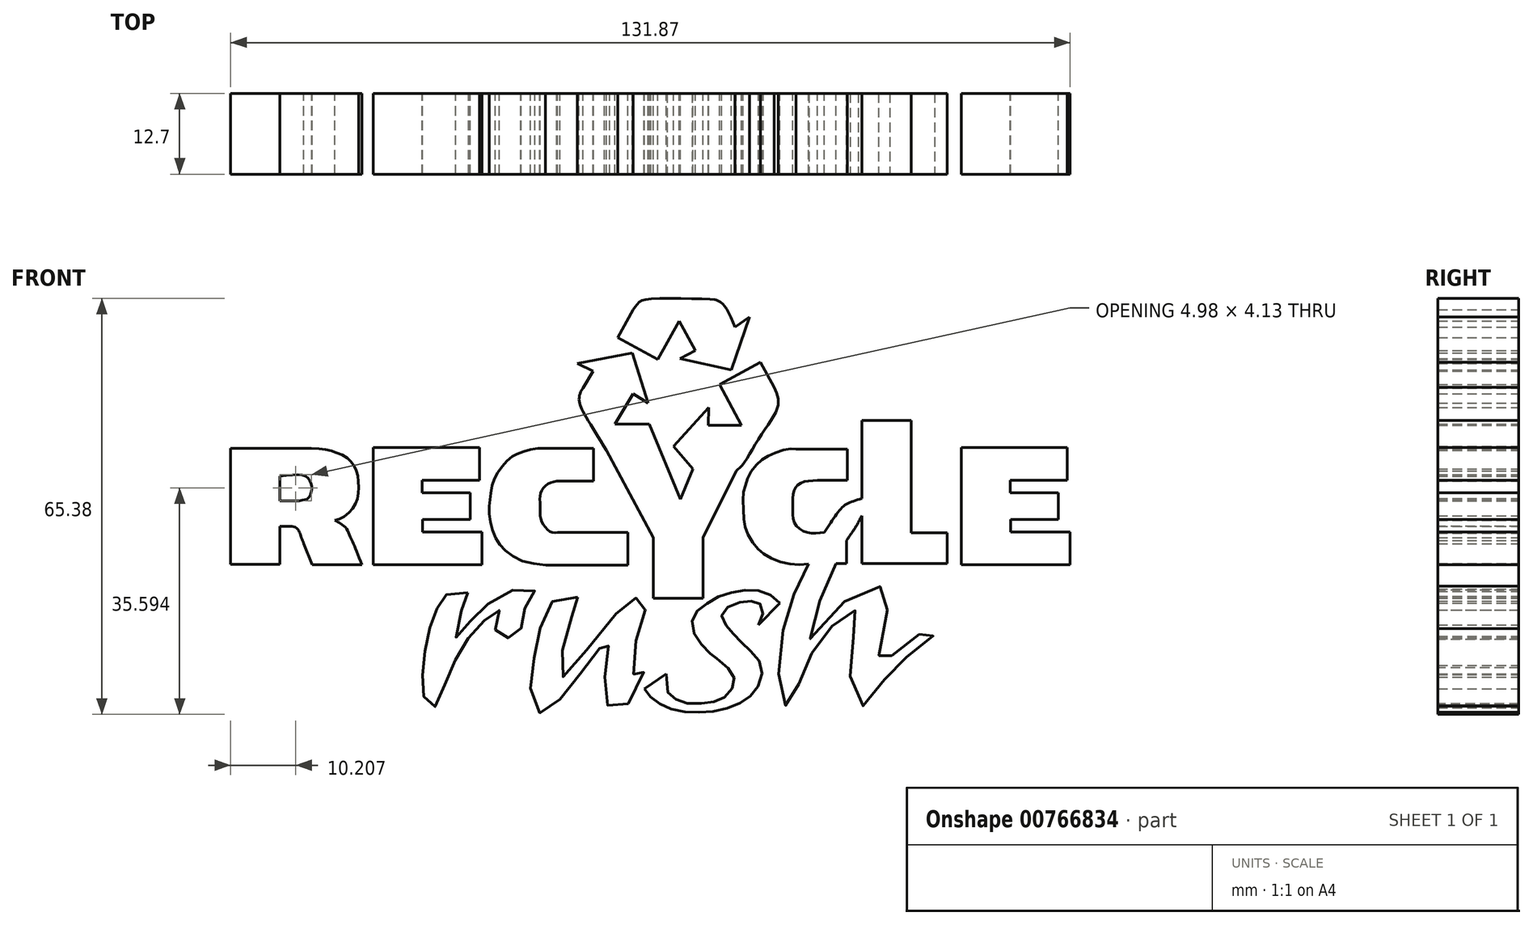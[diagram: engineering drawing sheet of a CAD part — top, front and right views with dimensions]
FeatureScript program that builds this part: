
annotation { "Feature Type Name" : "Feature", "Feature Type Description" : "" }
export const myFeature = defineFeature(function(context is Context, id is Id, definition is map)
    precondition{}
    {
        {
            var Q0;
            Q0=qCreatedBy(makeId("Front.planeOp"),FACE);
            var sketch = newSketch(context, id + "F0", { "sketchPlane" : qUnion([Q0])});
            skLineSegment(sketch, "E0", {"start": v(-43.6, 9.28) * mm, "end": v(-43.6, -9.2) * mm});
            skLineSegment(sketch, "E1", {"start": v(-43.6, -9.2) * mm, "end": v(-26.5, -9.2) * mm});
            skLineSegment(sketch, "E2", {"start": v(-26.5, -9.2) * mm, "end": v(-26.5, -4.05) * mm});
            skLineSegment(sketch, "E3", {"start": v(-26.5, -4.05) * mm, "end": v(-35.84, -4.05) * mm});
            skLineSegment(sketch, "E4", {"start": v(-35.84, -4.05) * mm, "end": v(-35.84, -2.06) * mm});
            skLineSegment(sketch, "E5", {"start": v(-35.84, -2.06) * mm, "end": v(-28.36, -2.06) * mm});
            skLineSegment(sketch, "E6", {"start": v(-28.36, -2.06) * mm, "end": v(-28.36, 2.1) * mm});
            skLineSegment(sketch, "E7", {"start": v(-28.36, 2.1) * mm, "end": v(-35.92, 2.1) * mm});
            skLineSegment(sketch, "E8", {"start": v(-35.92, 2.1) * mm, "end": v(-35.92, 4.09) * mm});
            skLineSegment(sketch, "E9", {"start": v(-35.92, 4.09) * mm, "end": v(-26.93, 4.09) * mm});
            skLineSegment(sketch, "E10", {"start": v(-26.93, 4.09) * mm, "end": v(-26.93, 9.28) * mm});
            skLineSegment(sketch, "E11", {"start": v(-26.93, 9.28) * mm, "end": v(-43.6, 9.28) * mm});
            skLineSegment(sketch, "E12.bottom", {"start": v(-66, 9.1) * mm, "end": v(-58.27, 9.1) * mm});
            skLineSegment(sketch, "E12.top", {"start": v(-66, -9.07) * mm, "end": v(-58.27, -9.07) * mm});
            skLineSegment(sketch, "E12.left", {"start": v(-66, 9.1) * mm, "end": v(-66, -9.07) * mm});
            skLineSegment(sketch, "E12.right", {"start": v(-58.27, 4.77) * mm, "end": v(-58.27, 0.85) * mm});
            skFitSpline(sketch, "E13", {"points": [v(-58.27, 9.1) * mm, v(-52.92, 9.1) * mm, v(-50.76, 8.84) * mm, v(-49.14, 8.37) * mm, v(-47.62, 7.56) * mm, v(-46.68, 6.41) * mm, v(-46.14, 5.26) * mm, v(-45.92, 3.68) * mm, v(-45.94, 1.98) * mm, v(-46.33, 0.53) * mm, v(-47.14, -0.7) * mm, v(-48.51, -1.8) * mm, v(-49.61, -2.21) * mm], "startDerivative": vector(42.38, 0.73) * mm, "endDerivative": vector(-16, -4.77) * mm});
            skFitSpline(sketch, "E14", {"points": [v(-49.61, -2.21) * mm, v(-48.87, -2.63) * mm, v(-47.91, -3.37) * mm, v(-47.2, -4.77) * mm, v(-46.68, -5.9) * mm, v(-45.37, -9.2) * mm], "startDerivative": vector(4.88, -2.66) * mm, "endDerivative": vector(4.84, -12.6) * mm});
            skLineSegment(sketch, "E15", {"start": v(-45.37, -9.2) * mm, "end": v(-53.2, -9.2) * mm});
            skLineSegment(sketch, "E16", {"start": v(-53.2, -9.2) * mm, "end": v(-54.52, -5.88) * mm});
            skFitSpline(sketch, "E17", {"points": [v(-54.52, -5.88) * mm, v(-54.98, -4.62) * mm, v(-55.4, -3.68) * mm, v(-56.17, -3.2) * mm, v(-57.92, -3.13) * mm, v(-58.27, -3.13) * mm], "startDerivative": vector(-2.08, 5.74) * mm, "endDerivative": vector(-2.94, 0.06) * mm});
            skFitSpline(sketch, "E18", {"points": [v(-58.27, 4.77) * mm, v(-54.52, 4.85) * mm, v(-53.57, 4.1) * mm, v(-53.26, 3.08) * mm, v(-53.47, 1.8) * mm, v(-53.94, 1.19) * mm, v(-54.52, 1) * mm, v(-55.73, 0.85) * mm, v(-57.42, 0.87) * mm, v(-58.27, 0.85) * mm], "startDerivative": vector(23.7, 2.7) * mm, "endDerivative": vector(-9.58, -0.43) * mm});
            skLineSegment(sketch, "E19.trimOffspring", {"start": v(-58.27, -3.13) * mm, "end": v(-58.27, -9.07) * mm});
            skLineSegment(sketch, "E20.bottom", {"start": v(33.14, 13.48) * mm, "end": v(40.9, 13.48) * mm});
            skLineSegment(sketch, "E20.top", {"start": v(33.14, -8.98) * mm, "end": v(40.9, -8.98) * mm});
            skLineSegment(sketch, "E20.left", {"start": v(33.14, 13.48) * mm, "end": v(33.14, 1.22) * mm});
            skLineSegment(sketch, "E20.right", {"start": v(40.9, 13.48) * mm, "end": v(40.9, -4.17) * mm});
            skLineSegment(sketch, "E21", {"start": v(40.9, -8.98) * mm, "end": v(46.6, -8.98) * mm});
            skLineSegment(sketch, "E22", {"start": v(46.6, -8.98) * mm, "end": v(46.6, -4.17) * mm});
            skLineSegment(sketch, "E23", {"start": v(46.6, -4.17) * mm, "end": v(40.9, -4.17) * mm});
            skLineSegment(sketch, "E24", {"start": v(30.78, -5.33) * mm, "end": v(30.78, -8.99) * mm});
            skLineSegment(sketch, "E25", {"start": v(30.78, -8.99) * mm, "end": v(29.13, -8.99) * mm});
            skFitSpline(sketch, "E26", {"points": [v(30.78, -5.33) * mm, v(31.51, -4.25) * mm, v(32.32, -3.02) * mm, v(33.14, -1.52) * mm], "startDerivative": vector(2.32, 3.42) * mm, "endDerivative": vector(2.26, 4.32) * mm});
            skFitSpline(sketch, "E27", {"points": [v(33.14, 1.22) * mm, v(31.44, 0.68) * mm, v(30.24, 0) * mm, v(29, -1.48) * mm, v(27.28, -4.1) * mm], "startDerivative": vector(-7.59, -2.16) * mm, "endDerivative": vector(-5.73, -8.86) * mm});
            skFitSpline(sketch, "E28", {"points": [v(27.28, -4.1) * mm, v(24.56, -4.1) * mm, v(22.57, -2.57) * mm, v(22.3, 0) * mm, v(22.43, 2.28) * mm, v(23.54, 3.67) * mm, v(26.18, 4.09) * mm], "startDerivative": vector(-15.66, -2.03) * mm, "endDerivative": vector(16.66, 0.52) * mm});
            skLineSegment(sketch, "E29", {"start": v(26.18, 4.09) * mm, "end": v(30.9, 4.09) * mm});
            skLineSegment(sketch, "E30", {"start": v(30.9, 4.09) * mm, "end": v(30.9, 9) * mm});
            skLineSegment(sketch, "E31", {"start": v(30.9, 9) * mm, "end": v(22.84, 9) * mm});
            skFitSpline(sketch, "E32", {"points": [v(22.84, 9) * mm, v(21.65, 9) * mm, v(19.19, 8.28) * mm, v(17.44, 7.3) * mm, v(15.82, 5.55) * mm, v(14.93, 3.5) * mm, v(14.53, 1.72) * mm, v(14.61, -1.54) * mm, v(15.04, -3.88) * mm, v(16.58, -6.42) * mm, v(18.3, -7.81) * mm, v(21.6, -9.01) * mm, v(24.77, -9.06) * mm], "startDerivative": vector(-17.73, 2.05) * mm, "endDerivative": vector(32.25, 2.73) * mm});
            skLineSegment(sketch, "E33.trimOffspring", {"start": v(33.14, -1.52) * mm, "end": v(33.14, -8.98) * mm});
            skLineSegment(sketch, "E34", {"start": v(48.78, 9.28) * mm, "end": v(48.78, -9.2) * mm});
            skLineSegment(sketch, "E35", {"start": v(48.78, -9.2) * mm, "end": v(65.88, -9.2) * mm});
            skLineSegment(sketch, "E36", {"start": v(65.88, -9.2) * mm, "end": v(65.88, -4.05) * mm});
            skLineSegment(sketch, "E37", {"start": v(65.88, -4.05) * mm, "end": v(56.54, -4.05) * mm});
            skLineSegment(sketch, "E38", {"start": v(56.54, -4.05) * mm, "end": v(56.54, -2.06) * mm});
            skLineSegment(sketch, "E39", {"start": v(56.54, -2.06) * mm, "end": v(64.03, -2.06) * mm});
            skLineSegment(sketch, "E40", {"start": v(64.03, -2.06) * mm, "end": v(64.03, 2.1) * mm});
            skLineSegment(sketch, "E41", {"start": v(64.03, 2.1) * mm, "end": v(56.47, 2.1) * mm});
            skLineSegment(sketch, "E42", {"start": v(56.47, 2.1) * mm, "end": v(56.47, 4.09) * mm});
            skLineSegment(sketch, "E43", {"start": v(56.47, 4.09) * mm, "end": v(65.46, 4.09) * mm});
            skLineSegment(sketch, "E44", {"start": v(65.46, 4.09) * mm, "end": v(65.46, 9.28) * mm});
            skLineSegment(sketch, "E45", {"start": v(65.46, 9.28) * mm, "end": v(48.78, 9.28) * mm});
            skLineSegment(sketch, "E46", {"start": v(0.38, -14.46) * mm, "end": v(8.2, -14.46) * mm});
            skLineSegment(sketch, "E47", {"start": v(8.2, -14.46) * mm, "end": v(8.2, -4.93) * mm});
            skLineSegment(sketch, "E48", {"start": v(8.2, -4.93) * mm, "end": v(13.4, 5.55) * mm});
            skLineSegment(sketch, "E49", {"start": v(0.38, -14.46) * mm, "end": v(0.38, -4.93) * mm});
            skLineSegment(sketch, "E50", {"start": v(0.38, -4.93) * mm, "end": v(-6.92, 8.81) * mm});
            skLineSegment(sketch, "E51", {"start": v(-9.07, 21.26) * mm, "end": v(-11.55, 22.45) * mm});
            skLineSegment(sketch, "E52", {"start": v(-11.55, 22.45) * mm, "end": v(-2.92, 24.1) * mm});
            skLineSegment(sketch, "E53", {"start": v(-2.92, 24.1) * mm, "end": v(-0.4, 16.23) * mm});
            skLineSegment(sketch, "E54", {"start": v(-0.4, 16.23) * mm, "end": v(-2.76, 17.67) * mm});
            skLineSegment(sketch, "E55", {"start": v(6.62, 5.86) * mm, "end": v(3.56, 9.4) * mm});
            skLineSegment(sketch, "E56", {"start": v(3.56, 9.4) * mm, "end": v(9.12, 15.52) * mm});
            skLineSegment(sketch, "E57", {"start": v(9.12, 15.52) * mm, "end": v(9.05, 12.77) * mm});
            skLineSegment(sketch, "E58", {"start": v(13.26, 28.18) * mm, "end": v(15.53, 29.74) * mm});
            skLineSegment(sketch, "E59", {"start": v(15.53, 29.74) * mm, "end": v(12.64, 21.43) * mm});
            skLineSegment(sketch, "E60", {"start": v(12.64, 21.43) * mm, "end": v(4.57, 23.2) * mm});
            skLineSegment(sketch, "E61", {"start": v(4.57, 23.2) * mm, "end": v(6.99, 24.51) * mm});
            skLineSegment(sketch, "E62", {"start": v(6.99, 24.51) * mm, "end": v(4.46, 29.15) * mm});
            skLineSegment(sketch, "E63", {"start": v(4.46, 29.15) * mm, "end": v(1.09, 23.06) * mm});
            skLineSegment(sketch, "E64", {"start": v(1.09, 23.06) * mm, "end": v(-5.2, 26.55) * mm});
            skLineSegment(sketch, "E65", {"start": v(-5.2, 26.55) * mm, "end": v(-2.8, 30.92) * mm});
            skFitSpline(sketch, "E66", {"points": [v(-2.8, 30.92) * mm, v(-1.9, 32) * mm, v(0, 32.62) * mm, v(10.1, 32.48) * mm, v(10.37, 32.41) * mm, v(11.07, 32) * mm, v(11.97, 30.92) * mm, v(13.26, 28.18) * mm], "startDerivative": vector(7.55, 10.2) * mm, "endDerivative": vector(7.62, -17.7) * mm});
            skLineSegment(sketch, "E67", {"start": v(-2.76, 17.67) * mm, "end": v(-5.63, 12.96) * mm});
            skLineSegment(sketch, "E68", {"start": v(-5.63, 12.96) * mm, "end": v(-0.23, 12.96) * mm});
            skLineSegment(sketch, "E69", {"start": v(-0.23, 12.96) * mm, "end": v(4.65, 1.14) * mm});
            skLineSegment(sketch, "E70", {"start": v(4.65, 1.14) * mm, "end": v(6.62, 5.86) * mm});
            skLineSegment(sketch, "E71", {"start": v(-9.07, 21.26) * mm, "end": v(-10.66, 18.61) * mm});
            skFitSpline(sketch, "E72", {"points": [v(-10.66, 18.61) * mm, v(-11.08, 17.83) * mm, v(-11.23, 16.46) * mm, v(-10.66, 15) * mm, v(-6.92, 8.81) * mm], "startDerivative": vector(-3.02, -4.47) * mm, "endDerivative": vector(10.8, -16.46) * mm});
            skLineSegment(sketch, "E73", {"start": v(9.05, 12.77) * mm, "end": v(14.27, 12.77) * mm});
            skLineSegment(sketch, "E74", {"start": v(14.27, 12.77) * mm, "end": v(10.8, 19.12) * mm});
            skLineSegment(sketch, "E75", {"start": v(10.8, 19.12) * mm, "end": v(17.24, 22.62) * mm});
            skLineSegment(sketch, "E76", {"start": v(17.24, 22.62) * mm, "end": v(19.38, 18.68) * mm});
            skFitSpline(sketch, "E77", {"points": [v(19.38, 18.68) * mm, v(19.99, 17.12) * mm, v(19.77, 15.13) * mm, v(17.18, 10.97) * mm, v(14.48, 6.6) * mm, v(13.4, 5.55) * mm], "startDerivative": vector(4.81, -9.86) * mm, "endDerivative": vector(-7.04, -5.45) * mm});
            skLineSegment(sketch, "E78", {"start": v(-9, 4) * mm, "end": v(-9, 9.15) * mm});
            skLineSegment(sketch, "E79", {"start": v(-9, 9.15) * mm, "end": v(-16.56, 9.15) * mm});
            skLineSegment(sketch, "E80", {"start": v(-9, 4) * mm, "end": v(-14.75, 4) * mm});
            skLineSegment(sketch, "E81", {"start": v(-3.63, -4.1) * mm, "end": v(-3.63, -9.2) * mm});
            skLineSegment(sketch, "E82", {"start": v(-3.63, -9.2) * mm, "end": v(-16.5, -9.2) * mm});
            skLineSegment(sketch, "E83", {"start": v(-3.63, -4.1) * mm, "end": v(-14.63, -4.1) * mm});
            skFitSpline(sketch, "E84", {"points": [v(-14.63, -4.1) * mm, v(-15.53, -4.1) * mm, v(-16.47, -3.4) * mm, v(-17.16, -2.3) * mm, v(-17.4, -1.07) * mm, v(-17.4, 0.5) * mm, v(-17.36, 1.84) * mm, v(-16.86, 2.87) * mm, v(-16.05, 3.6) * mm, v(-14.75, 4) * mm], "startDerivative": vector(-9.51, -1.43) * mm, "endDerivative": vector(11.9, 2.65) * mm});
            skFitSpline(sketch, "E85", {"points": [v(-16.56, 9.15) * mm, v(-18.32, 9.04) * mm, v(-19.92, 8.6) * mm, v(-21.2, 8.17) * mm, v(-22.05, 7.6) * mm, v(-23.24, 6.43) * mm, v(-24.19, 5.01) * mm, v(-24.86, 3.59) * mm, v(-25.15, 1.83) * mm, v(-25.32, 0.61) * mm, v(-25.38, -1.06) * mm, v(-25.04, -3.08) * mm, v(-24.26, -5.2) * mm, v(-23.03, -6.7) * mm, v(-20.68, -8.39) * mm, v(-16.5, -9.2) * mm], "startDerivative": vector(-27.54, -0.28) * mm, "endDerivative": vector(44.63, -4.63) * mm});
            skFitSpline(sketch, "E86", {"points": [v(29.13, -8.99) * mm, v(27.62, -12.44) * mm, v(25.92, -16.62) * mm, v(24.87, -20.93) * mm, v(27.35, -17.66) * mm, v(32.06, -14) * mm, v(35.2, -12.57) * mm, v(36.83, -12.94) * mm, v(37.55, -14.38) * mm, v(37.07, -16.59) * mm, v(36.3, -20.27) * mm, v(35.9, -25.33) * mm, v(36.71, -24.65) * mm, v(38.24, -23.09) * mm, v(40.4, -21.3) * mm, v(42.76, -19.74) * mm, v(43.92, -19.22) * mm, v(44.58, -19.66) * mm, v(44.25, -20.5) * mm, v(42.09, -22.05) * mm, v(40.04, -23.82) * mm, v(38.7, -25.1) * mm, v(36.93, -27.03) * mm, v(34.94, -29.42) * mm, v(33.5, -31.3) * mm, v(31.95, -30.58) * mm, v(31.34, -27.09) * mm, v(31.4, -23.38) * mm, v(31.95, -20) * mm, v(32.59, -17.43) * mm, v(32.4, -16.47) * mm, v(31.5, -16.42) * mm, v(29.82, -17.38) * mm, v(28.2, -19.1) * mm, v(26.57, -21.1) * mm, v(25.14, -23.4) * mm, v(24.18, -25.3) * mm, v(23.18, -28.22) * mm, v(22.46, -30.75) * mm, v(21.65, -31.37) * mm, v(20.65, -30.8) * mm, v(20.17, -28.17) * mm, v(20.12, -24.64) * mm, v(20.7, -19.86) * mm, v(21.37, -17.28) * mm, v(22.57, -13.68) * mm, v(23.75, -10.96) * mm, v(24.77, -9.06) * mm], "startDerivative": vector(-58.73, -135.62) * mm, "endDerivative": vector(52.61, 93.78) * mm});
            skFitSpline(sketch, "E87", {"points": [v(2.43, -26.29) * mm, v(2.57, -27.75) * mm, v(2.64, -29.06) * mm, v(3.65, -30.14) * mm, v(5.68, -30.96) * mm, v(8.66, -30.89) * mm, v(10.75, -30.41) * mm, v(12.38, -29.2) * mm, v(13.12, -27.44) * mm, v(12.62, -25.92) * mm, v(10.26, -23.78) * mm, v(9.54, -23.31) * mm, v(7.91, -21.62) * mm, v(6.63, -19.46) * mm, v(6.76, -17.09) * mm, v(8.18, -15.74) * mm, v(10.35, -14.32) * mm, v(13.12, -13.44) * mm, v(15.96, -13.17) * mm, v(18.47, -13.7) * mm, v(20.3, -15.2) * mm], "startDerivative": vector(5.07, -36.06) * mm, "endDerivative": vector(32.32, -32.5) * mm});
            skLineSegment(sketch, "E88", {"start": v(20.3, -15.2) * mm, "end": v(16.9, -18.65) * mm});
            skLineSegment(sketch, "E89", {"start": v(2.43, -26.29) * mm, "end": v(-1.02, -28.66) * mm});
            skFitSpline(sketch, "E90", {"points": [v(-1.02, -28.66) * mm, v(0, -29.94) * mm, v(1.7, -31.16) * mm, v(4.2, -32.1) * mm, v(7.44, -32.38) * mm, v(10.55, -32.1) * mm, v(13.6, -31.08) * mm, v(15.71, -29.76) * mm, v(17.13, -27.75) * mm, v(17.38, -25.07) * mm, v(15.76, -22.84) * mm, v(14.05, -21.16) * mm, v(12.58, -19.6) * mm, v(11.43, -18.04) * mm, v(11.3, -16.55) * mm, v(13.4, -15.26) * mm, v(15.42, -14.92) * mm, v(16.98, -15.14) * mm, v(17.65, -16.55) * mm, v(16.9, -18.65) * mm], "startDerivative": vector(20.7, -29.89) * mm, "endDerivative": vector(-19.13, -40.14) * mm});
            skFitSpline(sketch, "E91", {"points": [v(-28.72, -13.56) * mm, v(-31.34, -13.56) * mm, v(-32.9, -14.55) * mm, v(-33.56, -16.05) * mm, v(-34.41, -18.14) * mm, v(-35.13, -21.02) * mm, v(-35.72, -24.36) * mm, v(-35.85, -27.3) * mm, v(-35.66, -29.8) * mm, v(-34.6, -31.56) * mm, v(-33.63, -31.23) * mm, v(-32.32, -27.9) * mm, v(-30.75, -24.3) * mm, v(-28.98, -21.15) * mm, v(-26.95, -18.73) * mm, v(-24.6, -16.7) * mm, v(-23.81, -16.31) * mm, v(-24.34, -18.14) * mm, v(-24.14, -20.17) * mm, v(-23.03, -20.63) * mm, v(-20.54, -20.3) * mm, v(-20.41, -18.4) * mm, v(-19.82, -16.18) * mm, v(-18.7, -13.7) * mm, v(-18.19, -13.17) * mm, v(-22.05, -13.24) * mm, v(-25.65, -15.4) * mm, v(-27.94, -17.5) * mm, v(-30.49, -20.76) * mm, v(-30.3, -18.34) * mm, v(-28.98, -14.61) * mm, v(-28.72, -13.56) * mm]});
            skFitSpline(sketch, "E92", {"points": [v(-11.44, -14.27) * mm, v(-13.85, -14.41) * mm, v(-15.17, -14.76) * mm, v(-16.55, -16.18) * mm, v(-17.33, -18.88) * mm, v(-17.92, -21.39) * mm, v(-18.37, -23.94) * mm, v(-18.7, -26.3) * mm, v(-18.9, -29) * mm, v(-18.46, -31.06) * mm, v(-17.38, -32.48) * mm, v(-15.81, -32.14) * mm, v(-14.44, -30.56) * mm, v(-13.06, -28.75) * mm, v(-10.95, -26.15) * mm, v(-9.14, -23.7) * mm, v(-7.57, -21.73) * mm, v(-6.53, -20.4) * mm, v(-6.63, -21.88) * mm, v(-7.03, -24.13) * mm, v(-7.22, -27.28) * mm, v(-7.22, -29.58) * mm, v(-6.58, -31.7) * mm, v(-5.6, -32.68) * mm, v(-3.25, -30.76) * mm, v(-1.77, -29.34) * mm, v(-1.14, -24.97) * mm, v(-1.63, -25.6) * mm, v(-2.6, -26.44) * mm, v(-2.7, -24.43) * mm, v(-2.26, -20.94) * mm, v(-1.53, -18.49) * mm, v(-0.5, -15.5) * mm, v(0, -14.46) * mm, v(-2.72, -14.46) * mm, v(-3.78, -15.09) * mm, v(-5.11, -16.48) * mm, v(-8, -20.03) * mm, v(-12.69, -25.84) * mm, v(-13.63, -26.85) * mm, v(-14.2, -26.06) * mm, v(-14.14, -24) * mm, v(-13.41, -20.54) * mm, v(-12.46, -17.52) * mm, v(-11.85, -15.63) * mm, v(-11.62, -15.01) * mm, v(-11.44, -14.27) * mm]});
            skSolve(sketch);
        }
        {
            var Q0;
            Q0 = qSketchRegion(id + "F0", true);
            extrude(context, id + "F1", {"entities" : qUnion([Q0]), "depth" : 12.7 * mm, "offsetDistance" : 25.4 * mm});
        }
    });
